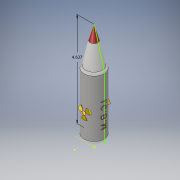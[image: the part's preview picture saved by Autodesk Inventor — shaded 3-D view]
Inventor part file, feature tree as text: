
AUTODESK INVENTOR PART (.ipt)
format: ipt  version: 2018 (Build 220112000, 112)  size: 540,672 bytes
history: native  units: in
note: dims shown in document units (in); Inventor stores cm internally (conversion verified against a paired STEP export)
features: plane x5, sketch x4, revolve x3, other x3, fillet x2, extrude x2, hole x1
ambient origin geometry x8: Origin, YZ Plane, XZ Plane, XY Plane, X Axis, Y Axis, Z Axis, Center Point
bodies: Solid1 (feature_tree)
feature tree (20):
  sketch  "Sketch1"  dims[d3=90.0deg d4=90.0deg]
  sketch  "Sketch2"  dims[d5=7.9375in d15=90.0deg d16=1.0in d17=0.0in]
  revolve  "Revolution2"  Angle=90.0deg
  revolve  "Revolution3"  Angle=90.0deg
  fillet  "Fillet1"  Radius=1.0in
  other  "Work Axis2"
  other  "Work Axis3"
  plane  "Work Plane2"
  plane  "Work Plane3"
  plane  "Work Plane4"
  plane  "Work Plane5"
  sketch  "Sketch3"  dims[d18=1.0in d19=0.0in d20=90.0deg]
  plane  "Work Plane6"
  extrude  "Extrusion1"  TaperAngle=90.0deg  [1 undecoded]
  extrude  "Extrusion2"  Depth=0.125in
  revolve  "Revolution4"  [1 undecoded]
  fillet  "Fillet4"  [1 undecoded]
  other  "Work Point2"
  hole  "Hole3"  [1 undecoded]
  sketch  "Sketch4"  dims[d29=4.6371in d31=0.125in d32=1.0in d33=1.0in d34=0.575in d35=0.75in d36=0.375in d37=0.25in d38=0.5635in d39=4.0in d40=0.8108in]
note: 4 required parameter values undecoded (feature->parameter linkage not recoverable at this tier; creation-order binding heuristic only, values carry confidence <= 0.55)
